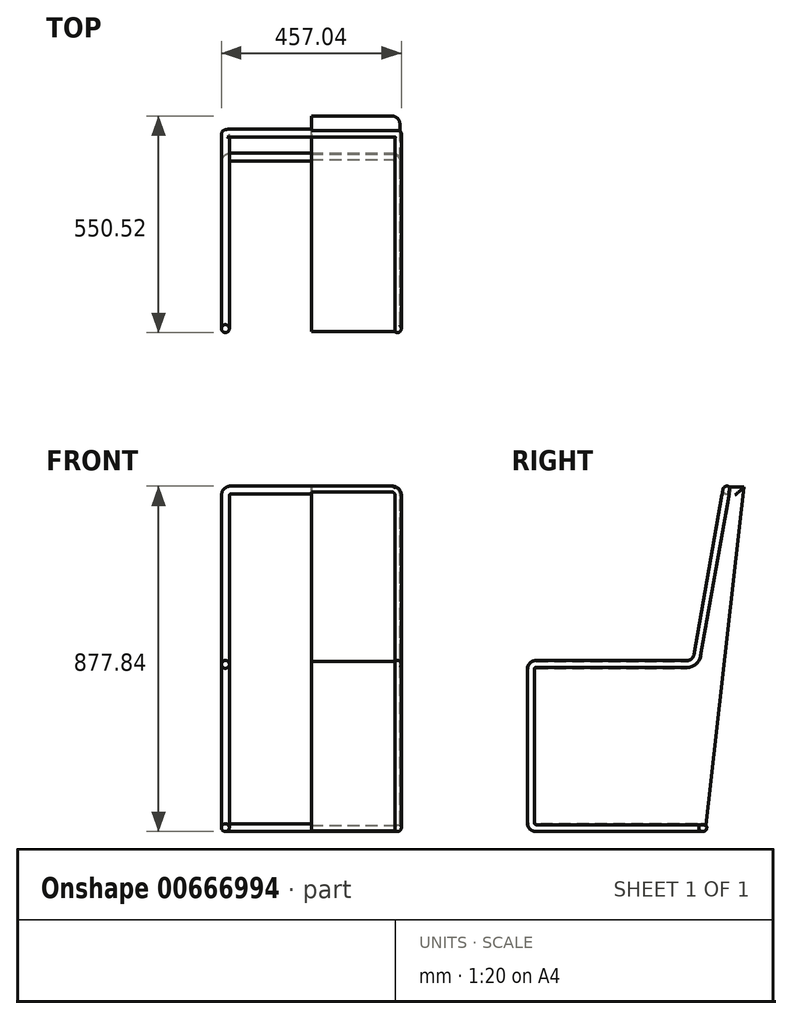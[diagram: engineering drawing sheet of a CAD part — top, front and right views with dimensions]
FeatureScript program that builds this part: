
annotation { "Feature Type Name" : "Feature", "Feature Type Description" : "" }
export const myFeature = defineFeature(function(context is Context, id is Id, definition is map)
    precondition{}
    {
        {
            var Q0;
            Q0=qCreatedBy(makeId("Right.planeOp"),FACE);
            var sketch = newSketch(context, id + "F0", { "sketchPlane" : qUnion([Q0])});
            skLineSegment(sketch, "E0", {"start": v(-450, 0) * mm, "end": v(-450, 430) * mm});
            skLineSegment(sketch, "E1", {"start": v(-450, 430) * mm, "end": v(-30, 430) * mm});
            skLineSegment(sketch, "E2", {"start": v(-30, 430) * mm, "end": v(48.14, 873.16) * mm});
            skLineSegment(sketch, "E3", {"start": v(48.14, 873.16) * mm, "end": v(98.14, 873.16) * mm});
            skLineSegment(sketch, "E4", {"start": v(98.14, 873.16) * mm, "end": v(0, 0) * mm});
            skLineSegment(sketch, "E5", {"start": v(-450, 0) * mm, "end": v(0, 0) * mm});
            skSolve(sketch);
        }
        {
            var Q0;
            Q0 = qSketchRegion(id + "F0", true);
            extrude(context, id + "F1", {"entities" : qUnion([Q0]), "depth" : 225 * mm, "offsetDistance" : 25 * mm});
        }
        {
            var Q0;
            Q0=makeQuery(id+"F1.opExtrude","SWEPT_EDGE",EDGE,{"disambiguationData":[OSD([sQuery(id+"F0.wireOp",EDGE,"E1"),sQuery(id+"F0.wireOp",EDGE,"E2")])]});
            var Q1;
            Q1=makeQuery(id+"F1.opExtrude","SWEPT_EDGE",EDGE,{"disambiguationData":[OSD([sQuery(id+"F0.wireOp",EDGE,"E0"),sQuery(id+"F0.wireOp",EDGE,"E1")])]});
            var Q2;
            Q2=makeQuery(id+"F1.opExtrude","CAP_EDGE",EDGE,{"disambiguationData":[OSD([sQuery(id+"F0.wireOp",EDGE,"E3")])],"isStart":false});
            var Q3;
            Q3=makeQuery(id+"F1.opExtrude","CAP_EDGE",EDGE,{"disambiguationData":[OSD([sQuery(id+"F0.wireOp",EDGE,"E4")])],"isStart":false});
            var Q4;
            Q4=makeQuery(id+"F1.opExtrude","SWEPT_EDGE",EDGE,{"disambiguationData":[OSD([sQuery(id+"F0.wireOp",EDGE,"E0"),sQuery(id+"F0.wireOp",EDGE,"E5")])]});
            fillet(context, id + "F2", {"entities" : qUnion([Q0, Q1, Q2, Q3, Q4]), "radius" : 20 * mm, "tangentPropagation" : true, "allowEdgeOverflow" : false});
        }
        {
            var Q0;
            Q0=makeQuery(id+"F1.opExtrude","CAP_FACE",FACE,{"disambiguationData":[OSD([sQuery(id+"F0.wireOp",EDGE,"E0"),sQuery(id+"F0.wireOp",EDGE,"E1"),sQuery(id+"F0.wireOp",EDGE,"E2"),sQuery(id+"F0.wireOp",EDGE,"E3"),sQuery(id+"F0.wireOp",EDGE,"E4"),sQuery(id+"F0.wireOp",EDGE,"E5")])],"isStart":false});
            var sketch = newSketch(context, id + "F3", { "sketchPlane" : qUnion([Q0])});
            skLineSegment(sketch, "E6.0", {"start": v(-27.09, 446.53) * mm, "end": v(44.62, 853.16) * mm});
            skArc(sketch, "E6.1", {"start": v(-27.09, 446.53) * mm, "mid": v(-33.93, 434.68) * mm, "end": v(-46.78, 430) * mm});
            skLineSegment(sketch, "E6.2", {"start": v(-430, 430) * mm, "end": v(-46.78, 430) * mm});
            skArc(sketch, "E6.3", {"start": v(-430, 430) * mm, "mid": v(-444.14, 424.14) * mm, "end": v(-450, 410) * mm});
            skLineSegment(sketch, "E6.4", {"start": v(-450, 20) * mm, "end": v(-450, 410) * mm});
            skArc(sketch, "E6.5", {"start": v(-450, 20) * mm, "mid": v(-444.14, 5.86) * mm, "end": v(-430, 0) * mm});
            skLineSegment(sketch, "E6.6", {"start": v(-430, 0) * mm, "end": v(-20.13, 0) * mm});
            skSolve(sketch);
        }
        {
            var Q0;
            Q0=makeQuery(id+"F1.opExtrude","SWEPT_FACE",FACE,{"disambiguationData":[OSD([sQuery(id+"F0.wireOp",EDGE,"E2")])]});
            var sketch = newSketch(context, id + "F4", { "sketchPlane" : qUnion([Q0])});
            skLineSegment(sketch, "E7.0", {"start": v(205, 868.26) * mm, "end": v(0, 868.26) * mm});
            skEllipticalArc(sketch, "E7.1", {});
            const initialGuessF4  = {"E7.1": [0.205, 0.8479493562275267, 0, 1, 0.020308532237714897, 0.02, 4.71238898038469, 0]};
            skSetInitialGuess(sketch, initialGuessF4);
            skSolve(sketch);
        }
        {
            var Q0;
            Q0=makeQuery(id+"F1.opExtrude","SWEPT_FACE",FACE,{"disambiguationData":[OSD([sQuery(id+"F0.wireOp",EDGE,"E5")])]});
            var sketch = newSketch(context, id + "F5", { "sketchPlane" : qUnion([Q0])});
            skLineSegment(sketch, "E8.0", {"start": v(205, 0) * mm, "end": v(0, 0) * mm});
            skEllipticalArc(sketch, "E8.1", {});
            const initialGuessF5  = {"E8.1": [0.205, 0.02012593621991215, 0, 1, 0.020125936219912058, 0.02, 3.141592653589793, 4.71238898038469]};
            skSetInitialGuess(sketch, initialGuessF5);
            skSolve(sketch);
        }
        {
            var Q0;
            Q0=qCreatedBy(makeId("Right.planeOp"),FACE);
            var sketch = newSketch(context, id + "F6", { "sketchPlane" : qUnion([Q0])});
            skCircle(sketch, "E9", {"center": v(-6.48, 7.62) * mm, "radius": 10 * mm});
            skSolve(sketch);
        }
        {
            var Q0;
            Q0 = qSketchRegion(id + "F6", true);
            var Q1;
            Q1=sQuery(id+"F5.wireOp",EDGE,"E8.0");
            var Q2;
            Q2=sQuery(id+"F5.wireOp",EDGE,"E8.1");
            var Q3;
            Q3=sQuery(id+"F3.wireOp",EDGE,"E6.6");
            var Q4;
            Q4=sQuery(id+"F3.wireOp",EDGE,"E6.5");
            var Q5;
            Q5=sQuery(id+"F3.wireOp",EDGE,"E6.4");
            var Q6;
            Q6=sQuery(id+"F3.wireOp",EDGE,"E6.3");
            var Q7;
            Q7=sQuery(id+"F3.wireOp",EDGE,"E6.2");
            var Q8;
            Q8=sQuery(id+"F3.wireOp",EDGE,"E6.1");
            var Q9;
            Q9=sQuery(id+"F3.wireOp",EDGE,"E6.0");
            var Q10;
            Q10=sQuery(id+"F4.wireOp",EDGE,"E7.1");
            var Q11;
            Q11=sQuery(id+"F4.wireOp",EDGE,"E7.0");
            sweep(context, id + "F7", {"profiles" : qUnion([Q0]), "path" : qUnion([Q1, Q2, Q3, Q4, Q5, Q6, Q7, Q8, Q9, Q10, Q11])});
        }
        {
            var Q0;
            Q0=makeQuery(id+"F7.opSweep","SWEPT_BODY",BODY,{"disambiguationData":[OSD([sQuery(id+"F4.wireOp",EDGE,"E7.0"),sQuery(id+"F6.wireOp",EDGE,"E9")])]});
            var Q1;
            Q1=qCreatedBy(makeId("Right.planeOp"),FACE);
            mirror(context, id + "F8", {"operationType" : NewBodyOperationType.ADD, "entities" : qUnion([Q0]), "mirrorPlane" : qUnion([Q1])});
        }
    });
